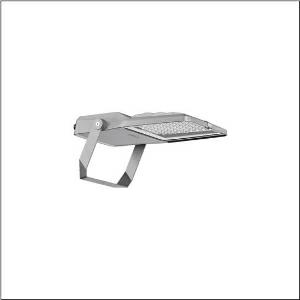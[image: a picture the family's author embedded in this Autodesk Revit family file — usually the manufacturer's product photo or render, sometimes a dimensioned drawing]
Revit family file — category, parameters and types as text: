
# Revit family: floodlight_fl_21_mini___pl52_5xa7772c2d1a_4fc0
name_source: partatom
category: Lighting Fixtures
units: mm (PartAtom-declared; Revit-internal decimal feet)

## family parameters
Cut with Voids When Loaded = No
Host = Face
Light Source = No
Part Type = Normal
Room Calculation Point = No
Round Connector Dimension = Use Diameter
Shared = No

## types (1)
- --- (1 x LED, 12210 lm, 87.2 W, 3000K)
    Apparent Load = 87 VA
    CIE Flux Codes = 26 60 98 100 100
    Color Rendering = 70
    Color Temperature = 3000K
    Default Elevation = 1800 mm
    Description = Floodlight FL 21 mini, floodlight, primary light control with lens, of PMMA, primary optical cover: protective disc, of toughened safety glass, transparent, light distribution: PL52, light emission: direct distribution, installation type: surface-mounted, LED, High Power LED, rated luminous flux: 12.210lm, luminous efficacy: 140lm/W, light colour: 730, colour temperature: 3000K, control gear: ECG iQ, control: Street-Remote, Auto-Match, Temp-Guard, Night-Set, Smart-Wire, Desk-Remote (wireless, voltage-free reading and setting of iQ features in the workshop via application-optimized NFC function/RFID function), optimised constant luminous flux control (CLO 2.0), with terminal, 6-pole, mains connection: 220..240V, AC, 50/60Hz, start of lifetime: 87W, end of lifetime: 92W, reduction: 40W, luminaire housing, of diecast aluminium, powder-coated, Siteco® metallic grey (DB 702S), corrosivity category C5 according to DIN EN ISO 12944, mounting bracket, of steel, galvanised, powder-coated, Siteco® metallic grey (DB 702S), protection rating (complete): IP66, insulation class (complete): insulation class II (safety insulation), certification: CE, ENEC, VDE, protection symbol: D, impact resistance: IK08, permissible operating ambient temperature: -40..+40°C, permissible operating ambient temperature for outdoor applications: -40..+50°C, standard: DIN EN 12944, packaging unit: 1 piece

Light Distribution: PL52
    Height = 70 mm
    Lamp = 1 x LED
    Lamp Light Flux = 12210 lm
    Lamp Power = 87.2 W
    Lamp count = 1
    Length = 485 mm
    Luminous efficacy = 140 lm/W
    Manufacturer = Siteco
    ModVariant = No
    Model = 5XA7772C2D1A
    Number of Poles = 1
    OnlyDefault = Yes
    Power Factor = 1
    Product Name = Floodlight FL 21 mini | PL52
    Product group = floodlight | pylon top
    ProductGroupID = 6101
    Protection Class = Protection class II
    Protection Degree = IP 66
    RLX_Detail_Level = 1
    RlxData = <blob elided: 96329 chars, md5=a837e1e0>
    Socket = socket
    Standby Power = 0 W
    System Light Flux = 12210 lm
    System Power = 87 W
    Type Comments = factory setting: luminous flux: 100 % | dim-lin: 254 | 456 mA
    Type Image = l_1006845.jpg
    URL = http://relux.com
    VarID = @adj_075495
    Voltage = 0 V
    Weight = 0.00 kg
    Width = 337 mm

## geometry (parser evidence)
native form markers: Blend x4, Sweep x12
no freeform markers — native parametric forms only
